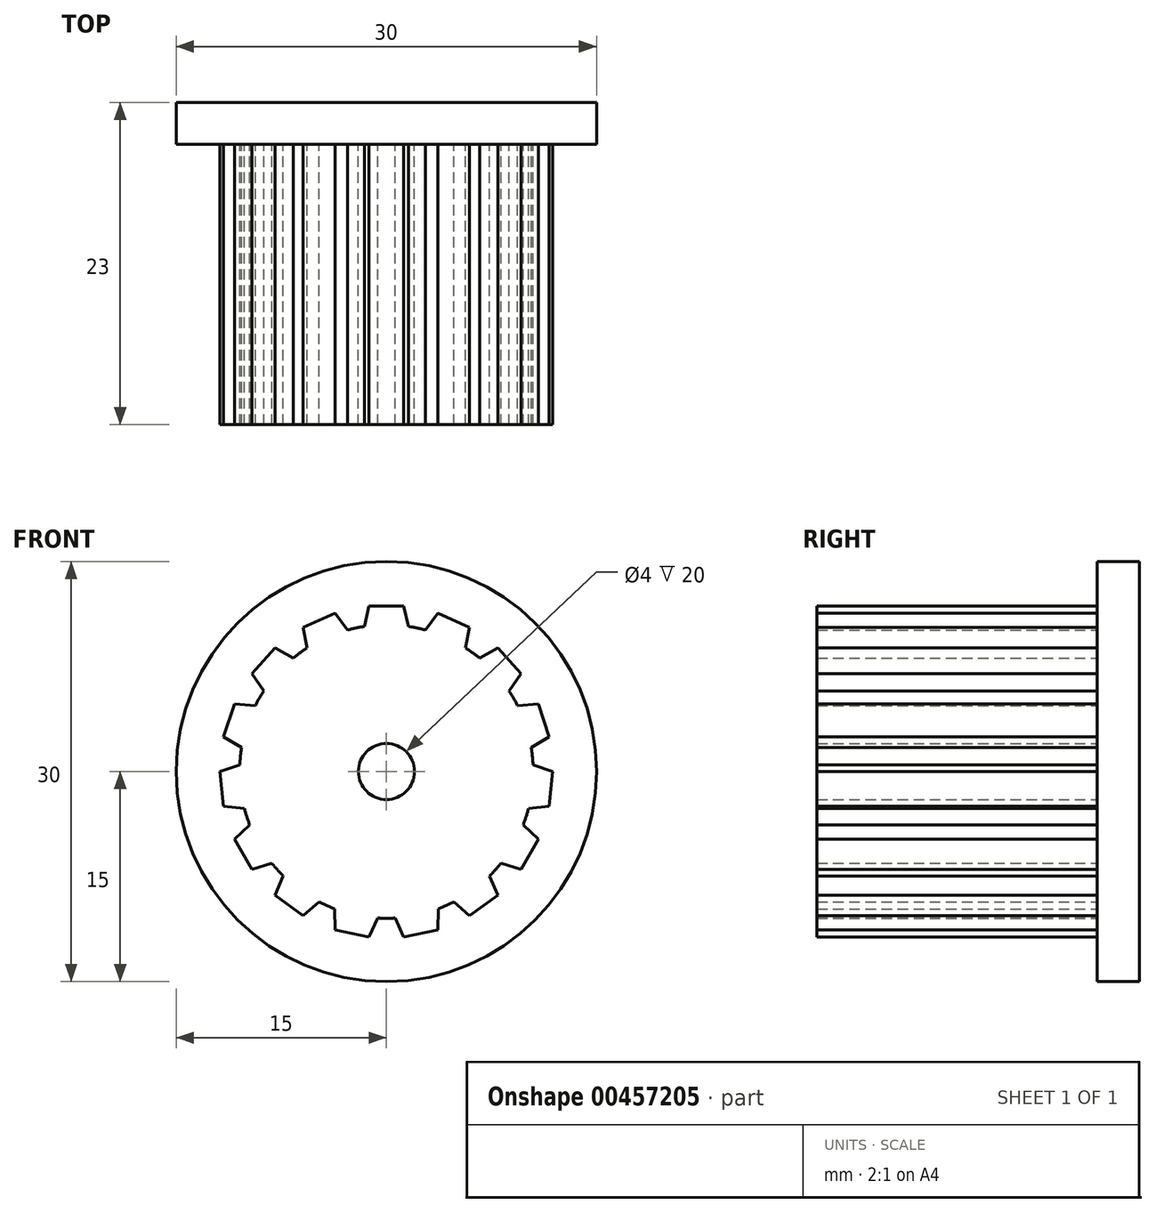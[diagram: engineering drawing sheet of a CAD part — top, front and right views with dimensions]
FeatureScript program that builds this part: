
annotation { "Feature Type Name" : "Feature", "Feature Type Description" : "" }
export const myFeature = defineFeature(function(context is Context, id is Id, definition is map)
    precondition{}
    {
        {
            var Q0;
            Q0=qCreatedBy(makeId("Front.planeOp"),FACE);
            var sketch = newSketch(context, id + "F0", { "sketchPlane" : qUnion([Q0])});
            skCircle(sketch, "E0", {"center": v(0, 0) * mm, "radius": 11.88 * mm, "construction": true});
            skLineSegment(sketch, "E1", {"start": v(0, 11.88) * mm, "end": v(0, 10.47) * mm, "construction": true});
            skCircle(sketch, "E2", {"center": v(0, 0) * mm, "radius": 10.47 * mm});
            skLineSegment(sketch, "E3", {"start": v(0, 0) * mm, "end": v(-1.24, 11.8) * mm, "construction": true});
            skLineSegment(sketch, "E4", {"start": v(0, 0) * mm, "end": v(-2.47, 11.62) * mm, "construction": true});
            skLineSegment(sketch, "E5.MirrorCS", {"start": v(0, 0) * mm, "end": v(1.24, 11.8) * mm, "construction": true});
            skLineSegment(sketch, "E6.MirrorCS", {"start": v(0, 0) * mm, "end": v(2.47, 11.62) * mm, "construction": true});
            skLineSegment(sketch, "E7", {"start": v(-1.24, 11.8) * mm, "end": v(1.24, 11.8) * mm});
            skLineSegment(sketch, "E8", {"start": v(-1.24, 11.8) * mm, "end": v(-1.58, 10.36) * mm});
            skLineSegment(sketch, "E9.MirrorCS", {"start": v(1.24, 11.8) * mm, "end": v(1.58, 10.36) * mm});
            skLineSegment(sketch, "E10.1.0", {"start": v(-5.94, 10.28) * mm, "end": v(-5.65, 8.82) * mm});
            skLineSegment(sketch, "E10.1.1", {"start": v(-5.94, 10.28) * mm, "end": v(-3.67, 11.3) * mm});
            skLineSegment(sketch, "E10.1.2", {"start": v(-3.67, 11.3) * mm, "end": v(-2.77, 10.1) * mm});
            skLineSegment(sketch, "E10.2.0", {"start": v(-9.6, 6.98) * mm, "end": v(-8.75, 5.76) * mm});
            skLineSegment(sketch, "E10.2.1", {"start": v(-9.6, 6.98) * mm, "end": v(-7.95, 8.82) * mm});
            skLineSegment(sketch, "E10.2.2", {"start": v(-7.95, 8.82) * mm, "end": v(-6.64, 8.1) * mm});
            skLineSegment(sketch, "E10.3.0", {"start": v(-11.62, 2.47) * mm, "end": v(-10.34, 1.7) * mm});
            skLineSegment(sketch, "E10.3.1", {"start": v(-11.62, 2.47) * mm, "end": v(-10.85, 4.83) * mm});
            skLineSegment(sketch, "E10.3.2", {"start": v(-10.85, 4.83) * mm, "end": v(-9.36, 4.7) * mm});
            skLineSegment(sketch, "E10.4.0", {"start": v(-11.62, -2.47) * mm, "end": v(-10.13, -2.65) * mm});
            skLineSegment(sketch, "E10.4.1", {"start": v(-11.62, -2.47) * mm, "end": v(-11.88, 0) * mm});
            skLineSegment(sketch, "E10.4.2", {"start": v(-11.88, 0) * mm, "end": v(-10.46, 0.49) * mm});
            skLineSegment(sketch, "E10.5.0", {"start": v(-9.6, -6.98) * mm, "end": v(-8.18, -6.54) * mm});
            skLineSegment(sketch, "E10.5.1", {"start": v(-9.6, -6.98) * mm, "end": v(-10.85, -4.83) * mm});
            skLineSegment(sketch, "E10.5.2", {"start": v(-10.85, -4.83) * mm, "end": v(-9.76, -3.81) * mm});
            skLineSegment(sketch, "E10.6.0", {"start": v(-5.94, -10.28) * mm, "end": v(-4.81, -9.3) * mm});
            skLineSegment(sketch, "E10.6.1", {"start": v(-5.94, -10.28) * mm, "end": v(-7.95, -8.82) * mm});
            skLineSegment(sketch, "E10.6.2", {"start": v(-7.95, -8.82) * mm, "end": v(-7.36, -7.45) * mm});
            skLineSegment(sketch, "E10.7.0", {"start": v(-1.24, -11.8) * mm, "end": v(-0.61, -10.46) * mm});
            skLineSegment(sketch, "E10.7.1", {"start": v(-1.24, -11.8) * mm, "end": v(-3.67, -11.3) * mm});
            skLineSegment(sketch, "E10.7.2", {"start": v(-3.67, -11.3) * mm, "end": v(-3.7, -9.8) * mm});
            skLineSegment(sketch, "E10.8.0", {"start": v(3.67, -11.3) * mm, "end": v(3.7, -9.8) * mm});
            skLineSegment(sketch, "E10.8.1", {"start": v(3.67, -11.3) * mm, "end": v(1.24, -11.8) * mm});
            skLineSegment(sketch, "E10.8.2", {"start": v(1.24, -11.8) * mm, "end": v(0.61, -10.46) * mm});
            skLineSegment(sketch, "E10.9.0", {"start": v(7.95, -8.82) * mm, "end": v(7.36, -7.45) * mm});
            skLineSegment(sketch, "E10.9.1", {"start": v(7.95, -8.82) * mm, "end": v(5.94, -10.28) * mm});
            skLineSegment(sketch, "E10.9.2", {"start": v(5.94, -10.28) * mm, "end": v(4.81, -9.3) * mm});
            skLineSegment(sketch, "E11", {"start": v(0, 0) * mm, "end": v(0, 11.88) * mm, "construction": true});
            skCircle(sketch, "E12", {"center": v(0, 0) * mm, "radius": 2 * mm});
            skLineSegment(sketch, "E13.2.10.0", {"start": v(10.85, -4.83) * mm, "end": v(9.76, -3.81) * mm});
            skLineSegment(sketch, "E13.3.10.0", {"start": v(10.85, -4.83) * mm, "end": v(9.6, -6.98) * mm});
            skLineSegment(sketch, "E13.6.10.0", {"start": v(9.6, -6.98) * mm, "end": v(8.18, -6.54) * mm});
            skLineSegment(sketch, "E13.2.11.0", {"start": v(11.88, 0) * mm, "end": v(10.46, 0.49) * mm});
            skLineSegment(sketch, "E13.3.11.0", {"start": v(11.88, 0) * mm, "end": v(11.62, -2.47) * mm});
            skLineSegment(sketch, "E13.6.11.0", {"start": v(11.62, -2.47) * mm, "end": v(10.13, -2.65) * mm});
            skLineSegment(sketch, "E13.2.12.0", {"start": v(10.85, 4.83) * mm, "end": v(9.36, 4.7) * mm});
            skLineSegment(sketch, "E13.3.12.0", {"start": v(10.85, 4.83) * mm, "end": v(11.62, 2.47) * mm});
            skLineSegment(sketch, "E13.6.12.0", {"start": v(11.62, 2.47) * mm, "end": v(10.34, 1.7) * mm});
            skLineSegment(sketch, "E13.2.13.0", {"start": v(7.95, 8.82) * mm, "end": v(6.64, 8.1) * mm});
            skLineSegment(sketch, "E13.3.13.0", {"start": v(7.95, 8.82) * mm, "end": v(9.6, 6.98) * mm});
            skLineSegment(sketch, "E13.6.13.0", {"start": v(9.6, 6.98) * mm, "end": v(8.75, 5.76) * mm});
            skLineSegment(sketch, "E13.2.14.0", {"start": v(3.67, 11.3) * mm, "end": v(2.77, 10.1) * mm});
            skLineSegment(sketch, "E13.3.14.0", {"start": v(3.67, 11.3) * mm, "end": v(5.94, 10.28) * mm});
            skLineSegment(sketch, "E13.6.14.0", {"start": v(5.94, 10.28) * mm, "end": v(5.65, 8.82) * mm});
            skSolve(sketch);
        }
        {
            var Q0;
            Q0=qSketchRegion(id+"F0",true);
            extrude(context, id + "F1", {"entities" : qUnion([Q0]), "depth" : 20 * mm, "offsetDistance" : 25 * mm});
        }
        {
            var Q0;
            Q0=qCreatedBy(makeId("Front.planeOp"),FACE);
            var sketch = newSketch(context, id + "F2", { "sketchPlane" : qUnion([Q0])});
            skCircle(sketch, "E14", {"center": v(0, 0) * mm, "radius": 15 * mm});
            skSolve(sketch);
        }
        {
            var Q0;
            Q0=qSketchRegion(id+"F2",true);
            extrude(context, id + "F3", {"entities" : qUnion([Q0]), "operationType" : NewBodyOperationType.ADD, "depth" : -3 * mm, "offsetDistance" : 25 * mm});
        }
    });
